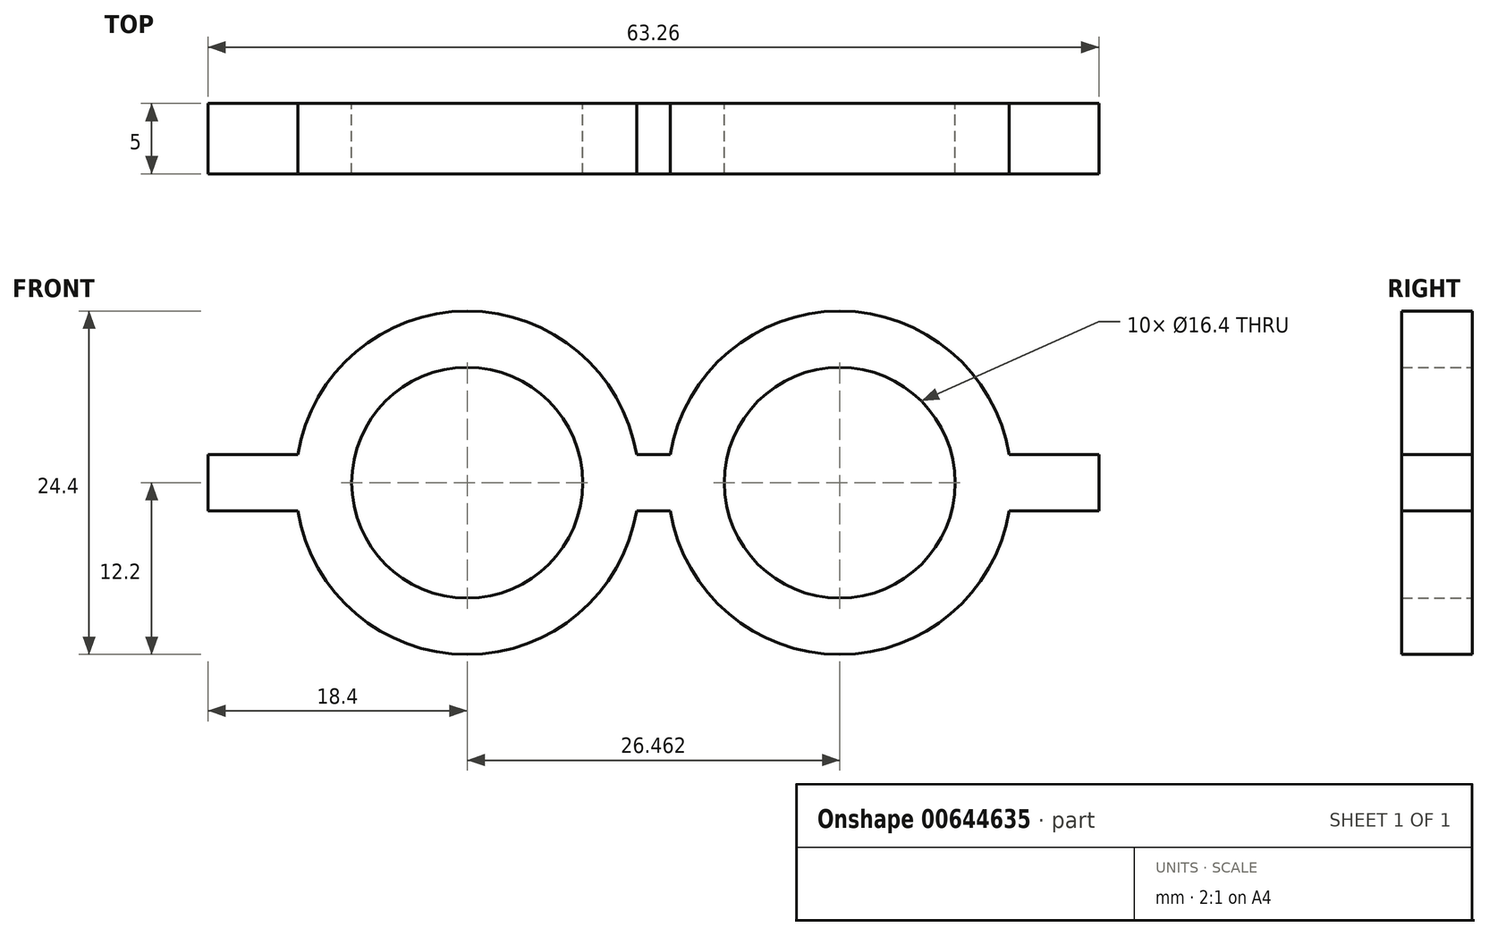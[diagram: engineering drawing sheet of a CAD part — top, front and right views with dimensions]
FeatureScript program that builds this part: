
annotation { "Feature Type Name" : "Feature", "Feature Type Description" : "" }
export const myFeature = defineFeature(function(context is Context, id is Id, definition is map)
    precondition{}
    {
        {
            var Q0;
            Q0=qCreatedBy(makeId("Front.planeOp"),FACE);
            var sketch = newSketch(context, id + "F0", { "sketchPlane" : qUnion([Q0])});
            skCircle(sketch, "E0", {"center": v(0, 0) * mm, "radius": 8.2 * mm});
            skArc(sketch, "E1.0", {"start": v(-12.03, -2) * mm, "mid": v(0, -12.2) * mm, "end": v(12.03, -2) * mm});
            skCircle(sketch, "E2", {"center": v(26.46, 0) * mm, "radius": 8.2 * mm});
            skArc(sketch, "E3.0", {"start": v(38.5, 2) * mm, "mid": v(26.46, 12.2) * mm, "end": v(14.43, 2) * mm});
            skLineSegment(sketch, "E4.bottom", {"start": v(14.43, -2) * mm, "end": v(12.03, -2) * mm});
            skLineSegment(sketch, "E4.top", {"start": v(14.43, 2) * mm, "end": v(12.03, 2) * mm});
            skPoint(sketch, "E4.middle", {"position": v(13.15, 0) * mm});
            skLineSegment(sketch, "E5.right", {"start": v(-18.4, -2) * mm, "end": v(-18.4, 2) * mm});
            skPoint(sketch, "E5.middle", {"position": v(-9.2, 0) * mm});
            skLineSegment(sketch, "E6.bottom", {"start": v(44.86, -2) * mm, "end": v(38.5, -2) * mm});
            skLineSegment(sketch, "E6.top", {"start": v(44.86, 2) * mm, "end": v(38.5, 2) * mm});
            skLineSegment(sketch, "E6.left", {"start": v(44.86, -2) * mm, "end": v(44.86, 2) * mm});
            skPoint(sketch, "E6.middle", {"position": v(35.66, 0) * mm});
            skPoint(sketch, "E6.middle.positionSnap0", {"position": v(17.76, 0) * mm});
            skPoint(sketch, "E6.centerSnap0", {"position": v(17.76, 0) * mm});
            skLineSegment(sketch, "E7.trimOffspring", {"start": v(-12.03, 2) * mm, "end": v(-18.4, 2) * mm});
            skLineSegment(sketch, "E8.trimOffspring", {"start": v(-12.03, -2) * mm, "end": v(-18.4, -2) * mm});
            skPoint(sketch, "E4.right.end.orphan", {"position": v(8.54, 2) * mm});
            skPoint(sketch, "E9.orphan", {"position": v(8.54, -2) * mm});
            skArc(sketch, "E10.trimOffspring", {"start": v(14.43, -2) * mm, "mid": v(26.46, -12.2) * mm, "end": v(38.5, -2) * mm});
            skArc(sketch, "E11.trimOffspring", {"start": v(12.03, 2) * mm, "mid": v(0, 12.2) * mm, "end": v(-12.03, 2) * mm});
            skPoint(sketch, "E4.left.end.orphan", {"position": v(17.76, 2) * mm});
            skPoint(sketch, "E12.orphan", {"position": v(17.76, -2) * mm});
            skPoint(sketch, "E13.orphan", {"position": v(26.46, -2) * mm});
            skPoint(sketch, "E6.right.end.orphan", {"position": v(26.46, 2) * mm});
            skPoint(sketch, "E14.orphan", {"position": v(0, 2) * mm});
            skPoint(sketch, "E5.left.start.orphan", {"position": v(0, -2) * mm});
            skSolve(sketch);
        }
        {
            var Q0;
            Q0=makeQuery(id+"F0.imprint","IMPRINT",FACE,{"disambiguationData":[TD([[makeQuery(id+"F0.imprint","IMPRINT",EDGE,{"derivedFrom":sQuery(id+"F0.wireOp",EDGE,"E0")}),-1.0]])]});
            extrude(context, id + "F1", {"entities" : qUnion([Q0]), "depth" : 5 * mm, "offsetDistance" : 25 * mm});
        }
    });
